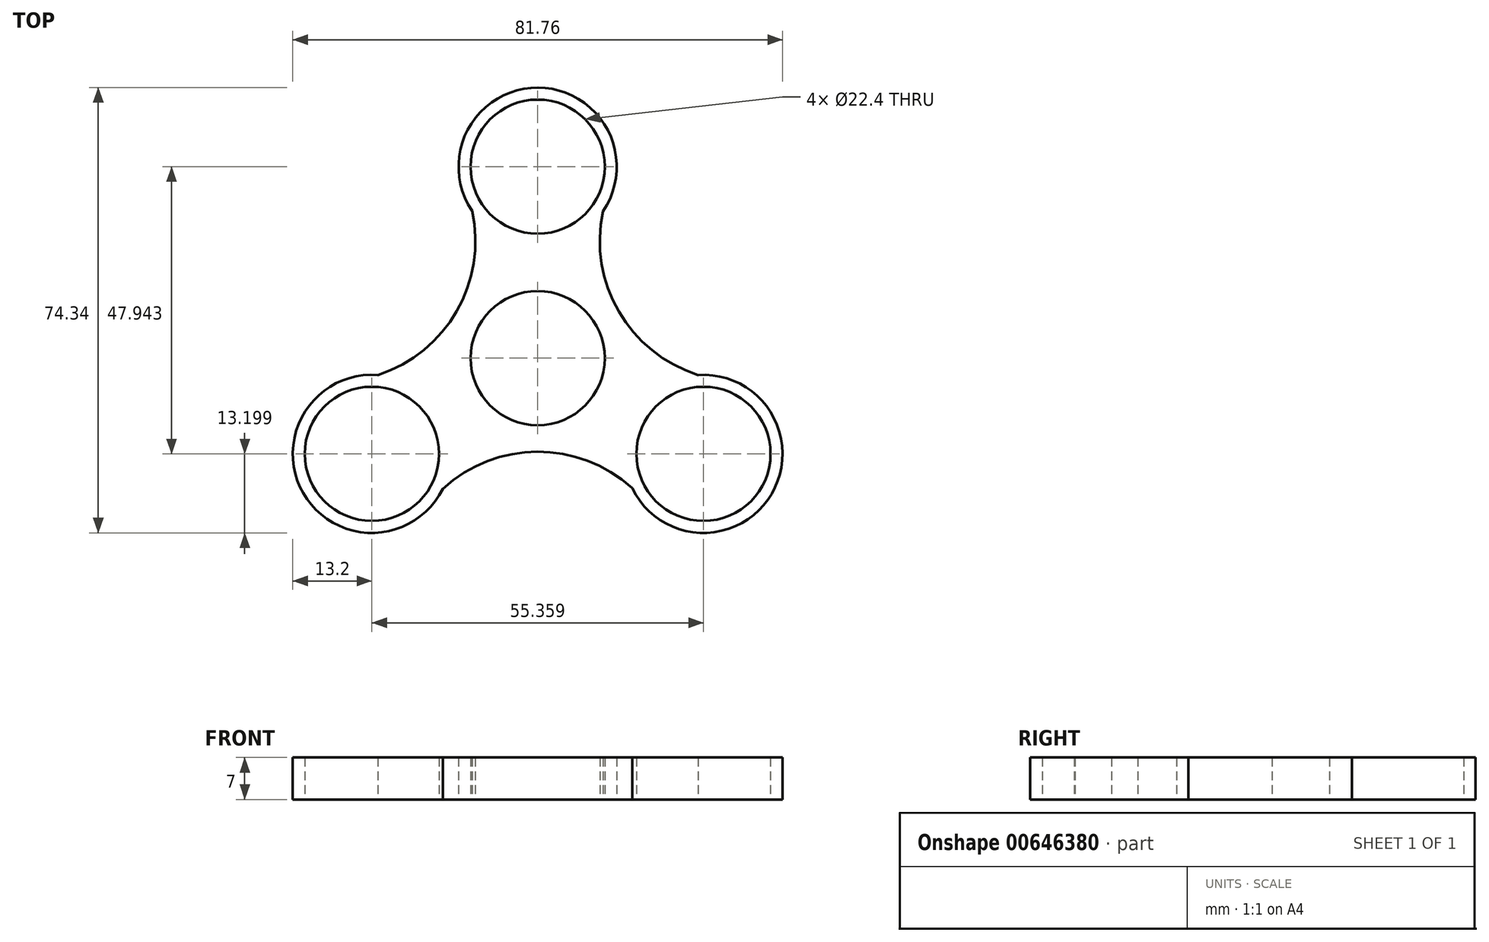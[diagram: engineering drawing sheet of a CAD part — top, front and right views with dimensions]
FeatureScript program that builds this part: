
annotation { "Feature Type Name" : "Feature", "Feature Type Description" : "" }
export const myFeature = defineFeature(function(context is Context, id is Id, definition is map)
    precondition{}
    {
        {
            var Q0;
            Q0=qCreatedBy(makeId("Top.planeOp"),FACE);
            var sketch = newSketch(context, id + "F0", { "sketchPlane" : qUnion([Q0])});
            skCircle(sketch, "E0", {"center": v(0, 0) * mm, "radius": 11.2 * mm});
            skCircle(sketch, "E1", {"center": v(0, 31.96) * mm, "radius": 11.2 * mm});
            skArc(sketch, "E2", {"start": v(10.9, 24.52) * mm, "mid": v(0.06, 45.16) * mm, "end": v(-10.97, 24.61) * mm});
            skCircle(sketch, "E3.1.0", {"center": v(-27.68, -15.98) * mm, "radius": 11.2 * mm});
            skArc(sketch, "E3.1.1", {"start": v(-26.68, -2.82) * mm, "mid": v(-39.14, -22.53) * mm, "end": v(-15.83, -21.8) * mm});
            skCircle(sketch, "E3.2.0", {"center": v(27.68, -15.98) * mm, "radius": 11.2 * mm});
            skArc(sketch, "E3.2.1", {"start": v(15.78, -21.7) * mm, "mid": v(39.08, -22.63) * mm, "end": v(26.8, -2.81) * mm});
            skArc(sketch, "E4", {"start": v(-26.68, -2.82) * mm, "mid": v(-13.5, 7.85) * mm, "end": v(-10.97, 24.61) * mm});
            skArc(sketch, "E5.1.0", {"start": v(15.78, -21.7) * mm, "mid": v(-0.05, -15.62) * mm, "end": v(-15.83, -21.8) * mm});
            skArc(sketch, "E5.2.0", {"start": v(10.9, 24.52) * mm, "mid": v(13.55, 7.77) * mm, "end": v(26.8, -2.81) * mm});
            skSolve(sketch);
        }
        {
            var Q0;
            Q0=makeQuery(id+"F0.imprint","IMPRINT",FACE,{"disambiguationData":[TD([[makeQuery(id+"F0.imprint","IMPRINT",EDGE,{"derivedFrom":sQuery(id+"F0.wireOp",EDGE,"E0")}),-1.0]])]});
            extrude(context, id + "F1", {"entities" : qUnion([Q0]), "depth" : 7 * mm, "offsetDistance" : 25 * mm});
        }
    });
